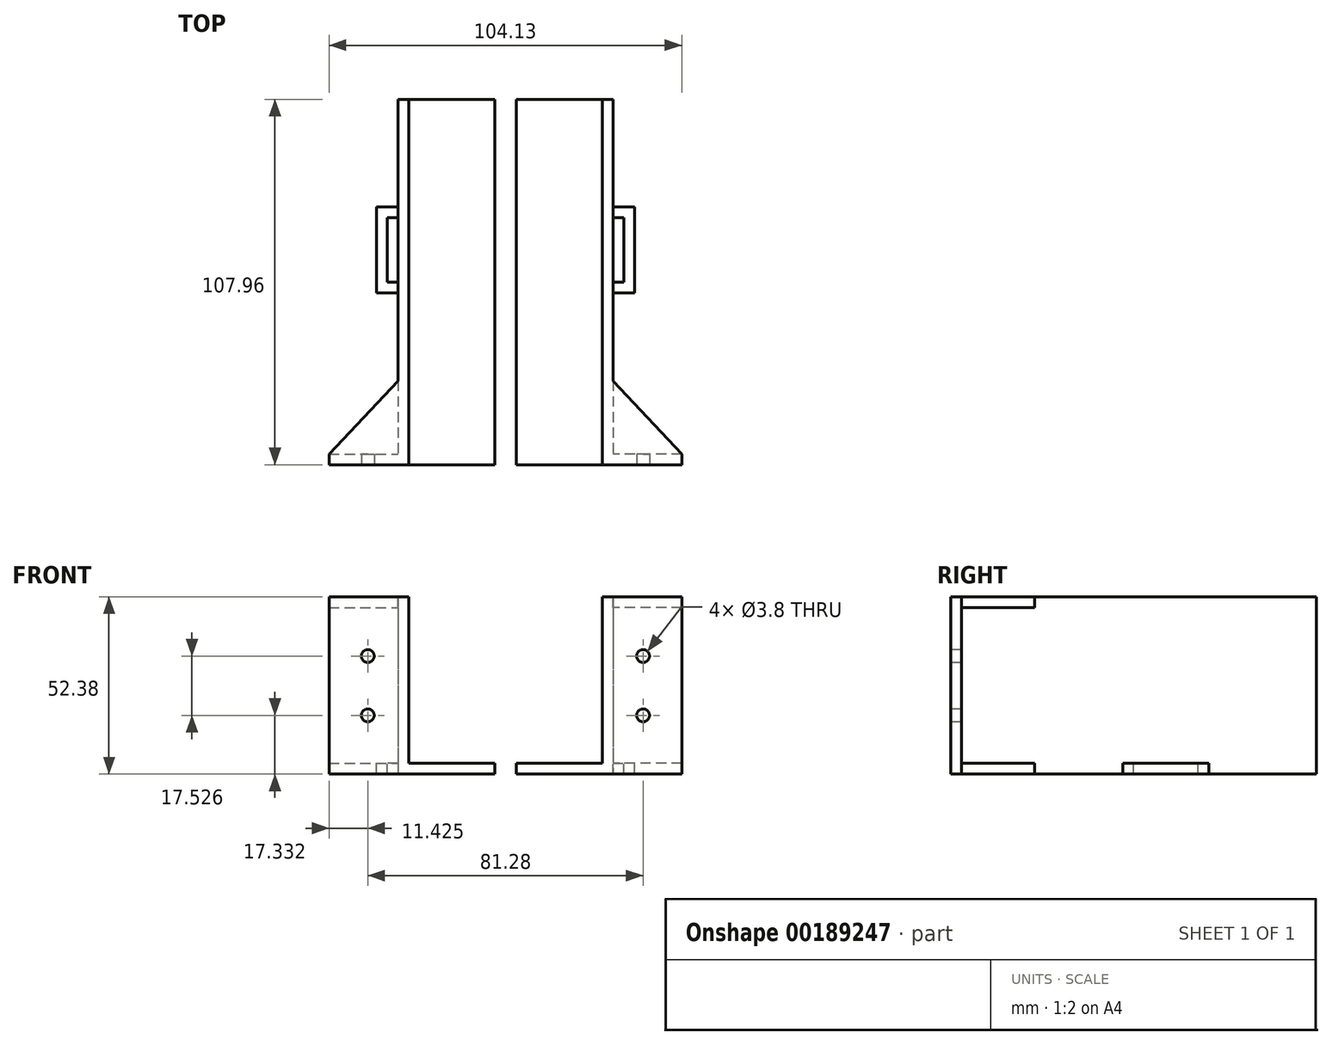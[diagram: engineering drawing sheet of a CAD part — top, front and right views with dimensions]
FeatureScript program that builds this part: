
annotation { "Feature Type Name" : "Feature", "Feature Type Description" : "" }
export const myFeature = defineFeature(function(context is Context, id is Id, definition is map)
    precondition{}
    {
        {
            var Q0;
            Q0=qCreatedBy(makeId("Right.planeOp"),FACE);
            var sketch = newSketch(context, id + "F0", { "sketchPlane" : qUnion([Q0])});
            skLineSegment(sketch, "E0.bottom", {"start": v(53.97, 26.2) * mm, "end": v(-53.98, 26.2) * mm});
            skLineSegment(sketch, "E0.top", {"start": v(53.98, -26.2) * mm, "end": v(-53.98, -26.2) * mm});
            skLineSegment(sketch, "E0.left", {"start": v(53.97, 26.2) * mm, "end": v(53.98, -26.2) * mm});
            skLineSegment(sketch, "E0.right", {"start": v(-53.98, 26.2) * mm, "end": v(-53.98, -26.2) * mm});
            skPoint(sketch, "E0.middle", {"position": v(0, 0) * mm});
            skSolve(sketch);
        }
        {
            var Q0;
            Q0 = qSketchRegion(id + "F0", true);
            extrude(context, id + "F1", {"entities" : qUnion([Q0]), "depth" : 3.17 * mm});
        }
        {
            var Q0;
            Q0=makeQuery(id+"F1.opExtrude","CAP_FACE",FACE,{"disambiguationData":[OSD([sQuery(id+"F0.wireOp",EDGE,"E0.bottom"),sQuery(id+"F0.wireOp",EDGE,"E0.top"),sQuery(id+"F0.wireOp",EDGE,"E0.left"),sQuery(id+"F0.wireOp",EDGE,"E0.right")])],"isStart":true});
            var sketch = newSketch(context, id + "F2", { "sketchPlane" : qUnion([Q0])});
            skLineSegment(sketch, "E1.bottom", {"start": v(-53.98, -26.2) * mm, "end": v(53.98, -26.2) * mm});
            skLineSegment(sketch, "E1.top", {"start": v(-53.98, -23.02) * mm, "end": v(53.98, -23.02) * mm});
            skLineSegment(sketch, "E1.left", {"start": v(-53.98, -26.2) * mm, "end": v(-53.98, -23.02) * mm});
            skLineSegment(sketch, "E1.right", {"start": v(53.98, -26.2) * mm, "end": v(53.98, -23.02) * mm});
            skSolve(sketch);
        }
        {
            var Q0;
            Q0 = qSketchRegion(id + "F2", true);
            extrude(context, id + "F3", {"entities" : qUnion([Q0]), "operationType" : NewBodyOperationType.ADD, "depth" : 25.4 * mm});
        }
        {
            var Q0;
            Q0=makeQuery(id+"F1.opExtrude","CAP_FACE",FACE,{"disambiguationData":[OSD([sQuery(id+"F0.wireOp",EDGE,"E0.bottom"),sQuery(id+"F0.wireOp",EDGE,"E0.top"),sQuery(id+"F0.wireOp",EDGE,"E0.left"),sQuery(id+"F0.wireOp",EDGE,"E0.right")])],"isStart":false});
            var sketch = newSketch(context, id + "F4", { "sketchPlane" : qUnion([Q0])});
            skLineSegment(sketch, "E2.bottom", {"start": v(-53.98, 26.2) * mm, "end": v(-50.8, 26.2) * mm});
            skLineSegment(sketch, "E2.top", {"start": v(-53.98, -26.2) * mm, "end": v(-50.8, -26.2) * mm});
            skLineSegment(sketch, "E2.left", {"start": v(-53.98, 26.2) * mm, "end": v(-53.98, -26.2) * mm});
            skLineSegment(sketch, "E2.right", {"start": v(-50.8, 26.2) * mm, "end": v(-50.8, -26.2) * mm});
            skSolve(sketch);
        }
        {
            var Q0;
            Q0 = qSketchRegion(id + "F4", true);
            extrude(context, id + "F5", {"entities" : qUnion([Q0]), "operationType" : NewBodyOperationType.ADD, "depth" : 20.32 * mm});
        }
        {
            var Q0;
            Q0=makeQuery(id+"F5.boolean.opBoolean","MERGE",FACE,{"derivedFrom":[makeQuery(id+"F3.boolean.opBoolean","MERGE",FACE,{"derivedFrom":[makeQuery(id+"F1.opExtrude","SWEPT_FACE",FACE,{"disambiguationData":[OSD([sQuery(id+"F0.wireOp",EDGE,"E0.top")])]}),makeQuery(id+"F3.opExtrude","SWEPT_FACE",FACE,{"disambiguationData":[OSD([sQuery(id+"F2.wireOp",EDGE,"E1.bottom")])]})]}),makeQuery(id+"F5.opExtrude","SWEPT_FACE",FACE,{"disambiguationData":[OSD([sQuery(id+"F4.wireOp",EDGE,"E2.top")])]})]});
            var sketch = newSketch(context, id + "F6", { "sketchPlane" : qUnion([Q0])});
            skLineSegment(sketch, "E3", {"start": v(23.5, 50.8) * mm, "end": v(3.17, 29.21) * mm});
            skLineSegment(sketch, "E4", {"start": v(3.17, 29.21) * mm, "end": v(3.18, 50.8) * mm});
            skLineSegment(sketch, "E5", {"start": v(3.18, 50.8) * mm, "end": v(23.5, 50.8) * mm});
            skSolve(sketch);
        }
        {
            var Q0;
            Q0 = qSketchRegion(id + "F6", true);
            extrude(context, id + "F7", {"entities" : qUnion([Q0]), "operationType" : NewBodyOperationType.ADD, "oppositeDirection" : true, "depth" : 3.17 * mm});
        }
        {
            var Q0;
            Q0=makeQuery(id+"F5.boolean.opBoolean","MERGE",FACE,{"derivedFrom":[makeQuery(id+"F1.opExtrude","SWEPT_FACE",FACE,{"disambiguationData":[OSD([sQuery(id+"F0.wireOp",EDGE,"E0.bottom")])]}),makeQuery(id+"F5.opExtrude","SWEPT_FACE",FACE,{"disambiguationData":[OSD([sQuery(id+"F4.wireOp",EDGE,"E2.bottom")])]})]});
            var sketch = newSketch(context, id + "F8", { "sketchPlane" : qUnion([Q0])});
            skLineSegment(sketch, "E6", {"start": v(23.5, -50.8) * mm, "end": v(3.17, -29.21) * mm});
            skLineSegment(sketch, "E7", {"start": v(3.18, -29.21) * mm, "end": v(3.18, -50.8) * mm});
            skLineSegment(sketch, "E8", {"start": v(3.18, -50.8) * mm, "end": v(23.5, -50.8) * mm});
            skSolve(sketch);
        }
        {
            var Q0;
            Q0 = qSketchRegion(id + "F8", true);
            extrude(context, id + "F9", {"entities" : qUnion([Q0]), "operationType" : NewBodyOperationType.ADD, "oppositeDirection" : true, "depth" : 3.17 * mm});
        }
        {
            var Q0;
            Q0=makeQuery(id+"F1.opExtrude","CAP_FACE",FACE,{"disambiguationData":[OSD([sQuery(id+"F0.wireOp",EDGE,"E0.bottom"),sQuery(id+"F0.wireOp",EDGE,"E0.top"),sQuery(id+"F0.wireOp",EDGE,"E0.left"),sQuery(id+"F0.wireOp",EDGE,"E0.right")])],"isStart":false});
            var sketch = newSketch(context, id + "F10", { "sketchPlane" : qUnion([Q0])});
            skLineSegment(sketch, "E9.bottom", {"start": v(-3.17, -26.2) * mm, "end": v(22.22, -26.2) * mm});
            skLineSegment(sketch, "E9.top", {"start": v(-3.18, -23.02) * mm, "end": v(22.23, -23.02) * mm});
            skLineSegment(sketch, "E9.left", {"start": v(-3.18, -26.2) * mm, "end": v(-3.18, -23.02) * mm});
            skLineSegment(sketch, "E9.right", {"start": v(22.23, -26.2) * mm, "end": v(22.23, -23.02) * mm});
            skSolve(sketch);
        }
        {
            var Q0;
            Q0 = qSketchRegion(id + "F10", true);
            extrude(context, id + "F11", {"entities" : qUnion([Q0]), "operationType" : NewBodyOperationType.ADD, "depth" : 6.35 * mm});
        }
        {
            var Q0;
            Q0=makeQuery(id+"F11.opExtrude","SWEPT_FACE",FACE,{"disambiguationData":[OSD([sQuery(id+"F10.wireOp",EDGE,"E9.top")])]});
            var sketch = newSketch(context, id + "F12", { "sketchPlane" : qUnion([Q0])});
            skLineSegment(sketch, "E10.bottom", {"start": v(3.18, 0) * mm, "end": v(6.35, 0) * mm});
            skLineSegment(sketch, "E10.top", {"start": v(3.17, 19.05) * mm, "end": v(6.35, 19.05) * mm});
            skLineSegment(sketch, "E10.left", {"start": v(3.18, 0) * mm, "end": v(3.18, 19.05) * mm});
            skLineSegment(sketch, "E10.right", {"start": v(6.35, 0) * mm, "end": v(6.35, 19.05) * mm});
            skSolve(sketch);
        }
        {
            var Q0;
            Q0 = qSketchRegion(id + "F12", true);
            extrude(context, id + "F13", {"entities" : qUnion([Q0]), "operationType" : NewBodyOperationType.REMOVE, "oppositeDirection" : true, "depth" : 25.4 * mm});
        }
        {
            var Q0;
            Q0=makeQuery(id+"F5.boolean.opBoolean","MERGE",FACE,{"derivedFrom":[makeQuery(id+"F3.boolean.opBoolean","MERGE",FACE,{"derivedFrom":[makeQuery(id+"F1.opExtrude","SWEPT_FACE",FACE,{"disambiguationData":[OSD([sQuery(id+"F0.wireOp",EDGE,"E0.right")])]}),makeQuery(id+"F3.opExtrude","SWEPT_FACE",FACE,{"disambiguationData":[OSD([sQuery(id+"F2.wireOp",EDGE,"E1.right")])]})]}),makeQuery(id+"F5.opExtrude","SWEPT_FACE",FACE,{"disambiguationData":[OSD([sQuery(id+"F4.wireOp",EDGE,"E2.left")])]})]});
            var sketch = newSketch(context, id + "F14", { "sketchPlane" : qUnion([Q0])});
            skPoint(sketch, "E11", {"position": v(12.07, 8.67) * mm});
            skPoint(sketch, "E12", {"position": v(12.07, -8.86) * mm});
            skSolve(sketch);
        }
        {
            var Q0;
            Q0=sQuery(id+"F14.wireOp",VERTEX,"E11");
            var Q1;
            Q1=sQuery(id+"F14.wireOp",VERTEX,"E12");
            var Q2;
            Q2=makeQuery(id+"F1.opExtrude","SWEPT_BODY",BODY,{"disambiguationData":[OSD([sQuery(id+"F0.wireOp",EDGE,"E0.bottom"),sQuery(id+"F0.wireOp",EDGE,"E0.top"),sQuery(id+"F0.wireOp",EDGE,"E0.left"),sQuery(id+"F0.wireOp",EDGE,"E0.right")])]});
            hole(context, id + "F15", {"style" : HoleStyle.SIMPLE, "endStyle" : HoleEndStyle.THROUGH, "standardTappedOrClearance" : lookupTablePath({ "standard" : "ANSI", "fit" : "Normal (ASME)", "size" : "#6", "type" : "Clearance" }), "standardBlindInLast" : lookupTablePath({ "fit" : "Free", "standard" : "ANSI", "size" : "#6", "type" : "Clearance" }), "holeDiameter" : 3.8 * mm, "locations" : qUnion([Q0, Q1]), "scope" : qUnion([Q2]), "isTappedThrough" : true});
        }
        {
            var Q0;
            Q0=makeQuery(id+"F3.opExtrude","CAP_FACE",FACE,{"disambiguationData":[OSD([sQuery(id+"F2.wireOp",EDGE,"E1.bottom"),sQuery(id+"F2.wireOp",EDGE,"E1.top"),sQuery(id+"F2.wireOp",EDGE,"E1.left"),sQuery(id+"F2.wireOp",EDGE,"E1.right")])],"isStart":false});
            cPlane(context, id + "F16", {"entities" : qUnion([Q0]), "cplaneType" : CPlaneType.OFFSET, "offset" : 3.17 * mm, "width" : 152.4 * mm, "height" : 152.4 * mm});
        }
        {
            var Q0;
            Q0=makeQuery(id+"F1.opExtrude","SWEPT_BODY",BODY,{"disambiguationData":[OSD([sQuery(id+"F0.wireOp",EDGE,"E0.bottom"),sQuery(id+"F0.wireOp",EDGE,"E0.top"),sQuery(id+"F0.wireOp",EDGE,"E0.left"),sQuery(id+"F0.wireOp",EDGE,"E0.right")])]});
            var Q1;
            Q1=qCreatedBy(id+"F16.planeOp",FACE);
            mirror(context, id + "F17", {"entities" : qUnion([Q0]), "mirrorPlane" : qUnion([Q1])});
        }
    });
